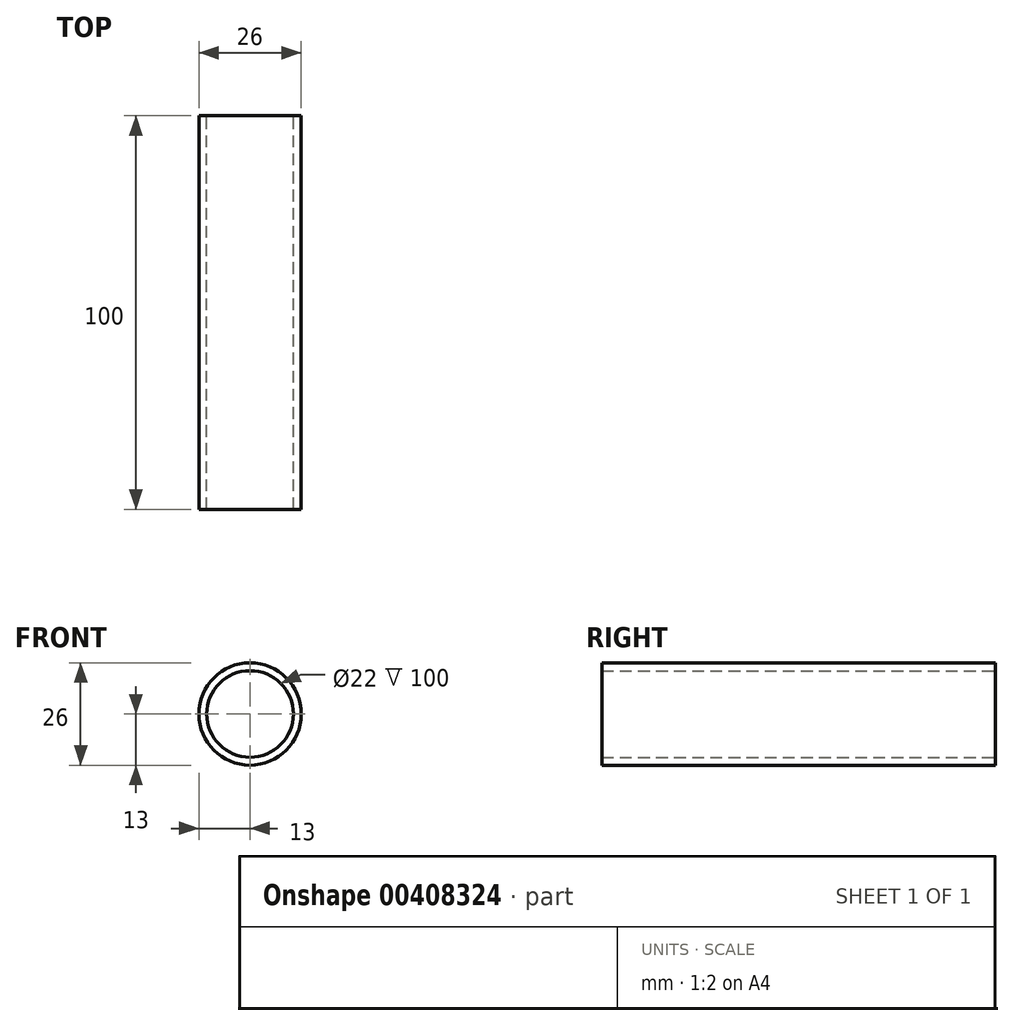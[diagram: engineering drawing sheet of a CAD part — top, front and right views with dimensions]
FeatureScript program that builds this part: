
annotation { "Feature Type Name" : "Feature", "Feature Type Description" : "" }
export const myFeature = defineFeature(function(context is Context, id is Id, definition is map)
    precondition{}
    {
        {
            var Q0;
            Q0=qCreatedBy(makeId("Front.planeOp"),FACE);
            var sketch = newSketch(context, id + "F0", { "sketchPlane" : qUnion([Q0])});
            skCircle(sketch, "E0", {"center": v(0, 0) * mm, "radius": 11 * mm});
            skCircle(sketch, "E1", {"center": v(0, 0) * mm, "radius": 13 * mm});
            skSolve(sketch);
        }
        {
            var Q0;
            Q0=makeQuery(id+"F0.imprint","IMPRINT",FACE,{"disambiguationData":[TD([[makeQuery(id+"F0.imprint","IMPRINT",EDGE,{"derivedFrom":sQuery(id+"F0.wireOp",EDGE,"E0")}),-1.0]])]});
            extrude(context, id + "F1", {"entities" : qUnion([Q0]), "depth" : 100 * mm});
        }
    });
